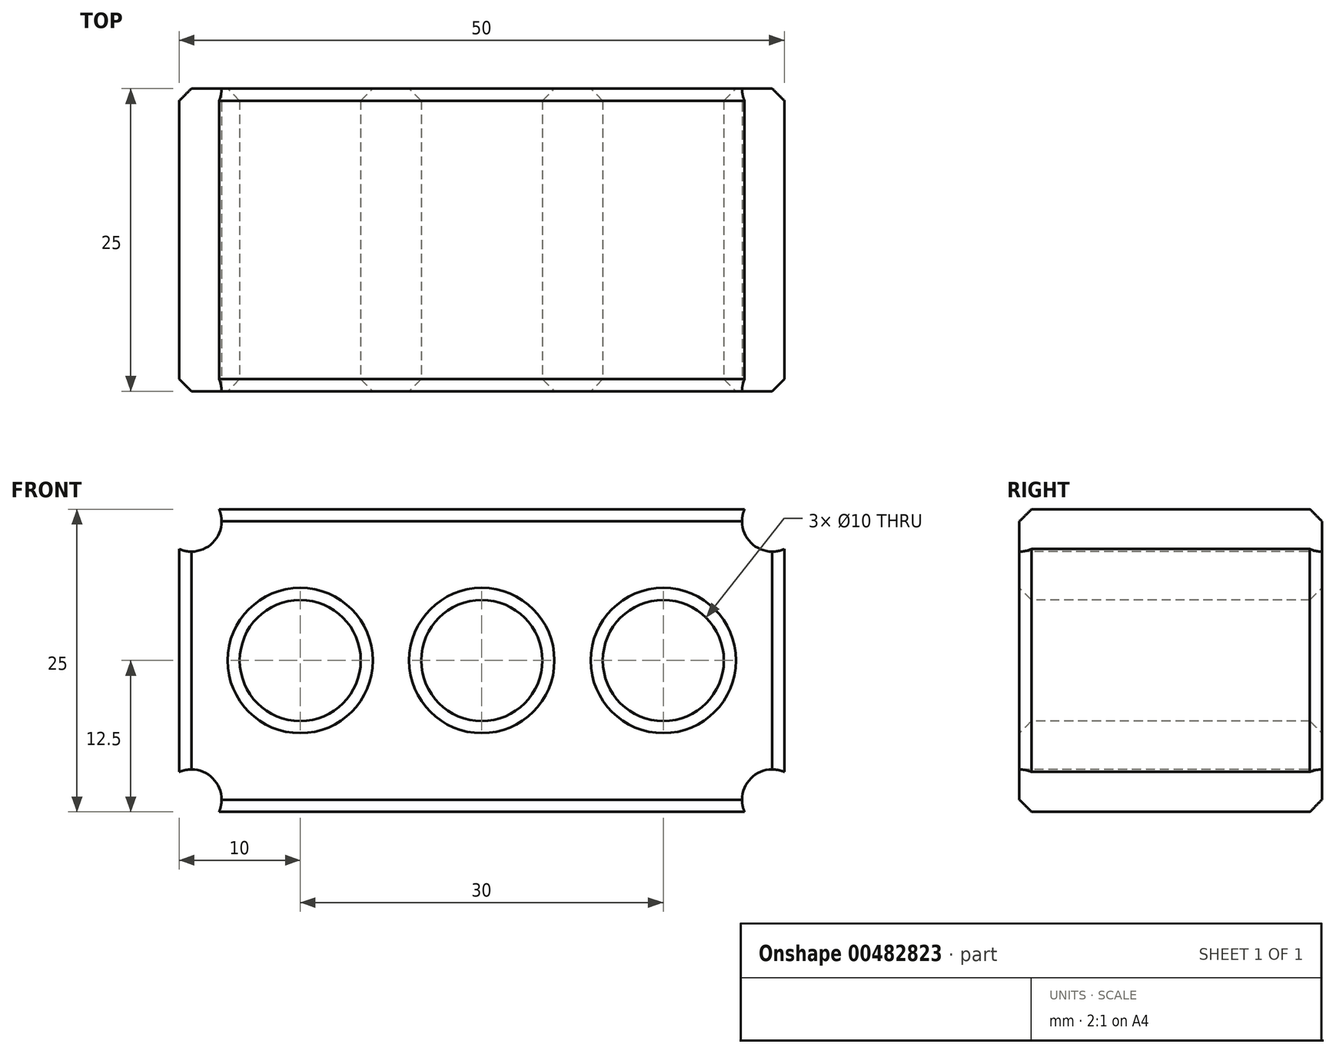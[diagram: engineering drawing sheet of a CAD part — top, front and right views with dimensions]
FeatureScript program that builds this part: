
annotation { "Feature Type Name" : "Feature", "Feature Type Description" : "" }
export const myFeature = defineFeature(function(context is Context, id is Id, definition is map)
    precondition{}
    {
        {
            var Q0;
            Q0=qCreatedBy(makeId("Front.planeOp"),FACE);
            var sketch = newSketch(context, id + "F0", { "sketchPlane" : qUnion([Q0])});
            skLineSegment(sketch, "E0.bottom", {"start": v(25, -12.5) * mm, "end": v(-25, -12.5) * mm});
            skLineSegment(sketch, "E0.top", {"start": v(25, 12.5) * mm, "end": v(-25, 12.5) * mm});
            skLineSegment(sketch, "E0.left", {"start": v(25, -12.5) * mm, "end": v(25, 12.5) * mm});
            skLineSegment(sketch, "E0.right", {"start": v(-25, -12.5) * mm, "end": v(-25, 12.5) * mm});
            skPoint(sketch, "E0.middle", {"position": v(0, 0) * mm});
            skSolve(sketch);
        }
        {
            var Q0;
            Q0 = qSketchRegion(id + "F0", true);
            extrude(context, id + "F1", {"entities" : qUnion([Q0]), "depth" : 25 * mm});
        }
        {
            var Q0;
            Q0=makeQuery(id+"F1.opExtrude","CAP_FACE",FACE,{"disambiguationData":[OSD([sQuery(id+"F0.wireOp",EDGE,"E0.bottom"),sQuery(id+"F0.wireOp",EDGE,"E0.top"),sQuery(id+"F0.wireOp",EDGE,"E0.left"),sQuery(id+"F0.wireOp",EDGE,"E0.right")])],"isStart":false});
            var sketch = newSketch(context, id + "F2", { "sketchPlane" : qUnion([Q0])});
            skCircle(sketch, "E1", {"center": v(0, 0) * mm, "radius": 5 * mm});
            skCircle(sketch, "E2", {"center": v(15, 0) * mm, "radius": 5 * mm});
            skCircle(sketch, "E3", {"center": v(-15, 0) * mm, "radius": 5 * mm});
            skSolve(sketch);
        }
        {
            var Q0;
            Q0 = qSketchRegion(id + "F2", true);
            extrude(context, id + "F3", {"entities" : qUnion([Q0]), "operationType" : NewBodyOperationType.REMOVE, "oppositeDirection" : true, "depth" : 25 * mm});
        }
        {
            var Q0;
            Q0=makeQuery(id+"F1.opExtrude","CAP_FACE",FACE,{"disambiguationData":[OSD([sQuery(id+"F0.wireOp",EDGE,"E0.bottom"),sQuery(id+"F0.wireOp",EDGE,"E0.top"),sQuery(id+"F0.wireOp",EDGE,"E0.left"),sQuery(id+"F0.wireOp",EDGE,"E0.right")])],"isStart":false});
            var Q1;
            Q1=makeQuery(id+"F1.opExtrude","CAP_FACE",FACE,{"disambiguationData":[OSD([sQuery(id+"F0.wireOp",EDGE,"E0.bottom"),sQuery(id+"F0.wireOp",EDGE,"E0.top"),sQuery(id+"F0.wireOp",EDGE,"E0.left"),sQuery(id+"F0.wireOp",EDGE,"E0.right")])],"isStart":true});
            chamfer(context, id + "F4", {"entities" : qUnion([Q0, Q1]), "width" : 1 * mm, "tangentPropagation" : true});
        }
        {
            var Q0;
            Q0=makeQuery(id+"F1.opExtrude","CAP_FACE",FACE,{"disambiguationData":[OSD([sQuery(id+"F0.wireOp",EDGE,"E0.bottom"),sQuery(id+"F0.wireOp",EDGE,"E0.top"),sQuery(id+"F0.wireOp",EDGE,"E0.left"),sQuery(id+"F0.wireOp",EDGE,"E0.right")])],"isStart":false});
            var sketch = newSketch(context, id + "F5", { "sketchPlane" : qUnion([Q0])});
            skCircle(sketch, "E4", {"center": v(-24, 11.5) * mm, "radius": 2.5 * mm});
            skCircle(sketch, "E5", {"center": v(24, 11.5) * mm, "radius": 2.5 * mm});
            skCircle(sketch, "E6", {"center": v(24, -11.5) * mm, "radius": 2.5 * mm});
            skCircle(sketch, "E7", {"center": v(-24, -11.5) * mm, "radius": 2.5 * mm});
            skSolve(sketch);
        }
        {
            var Q0;
            Q0 = qSketchRegion(id + "F5", true);
            extrude(context, id + "F6", {"entities" : qUnion([Q0]), "operationType" : NewBodyOperationType.REMOVE, "oppositeDirection" : true, "depth" : 25 * mm});
        }
    });
